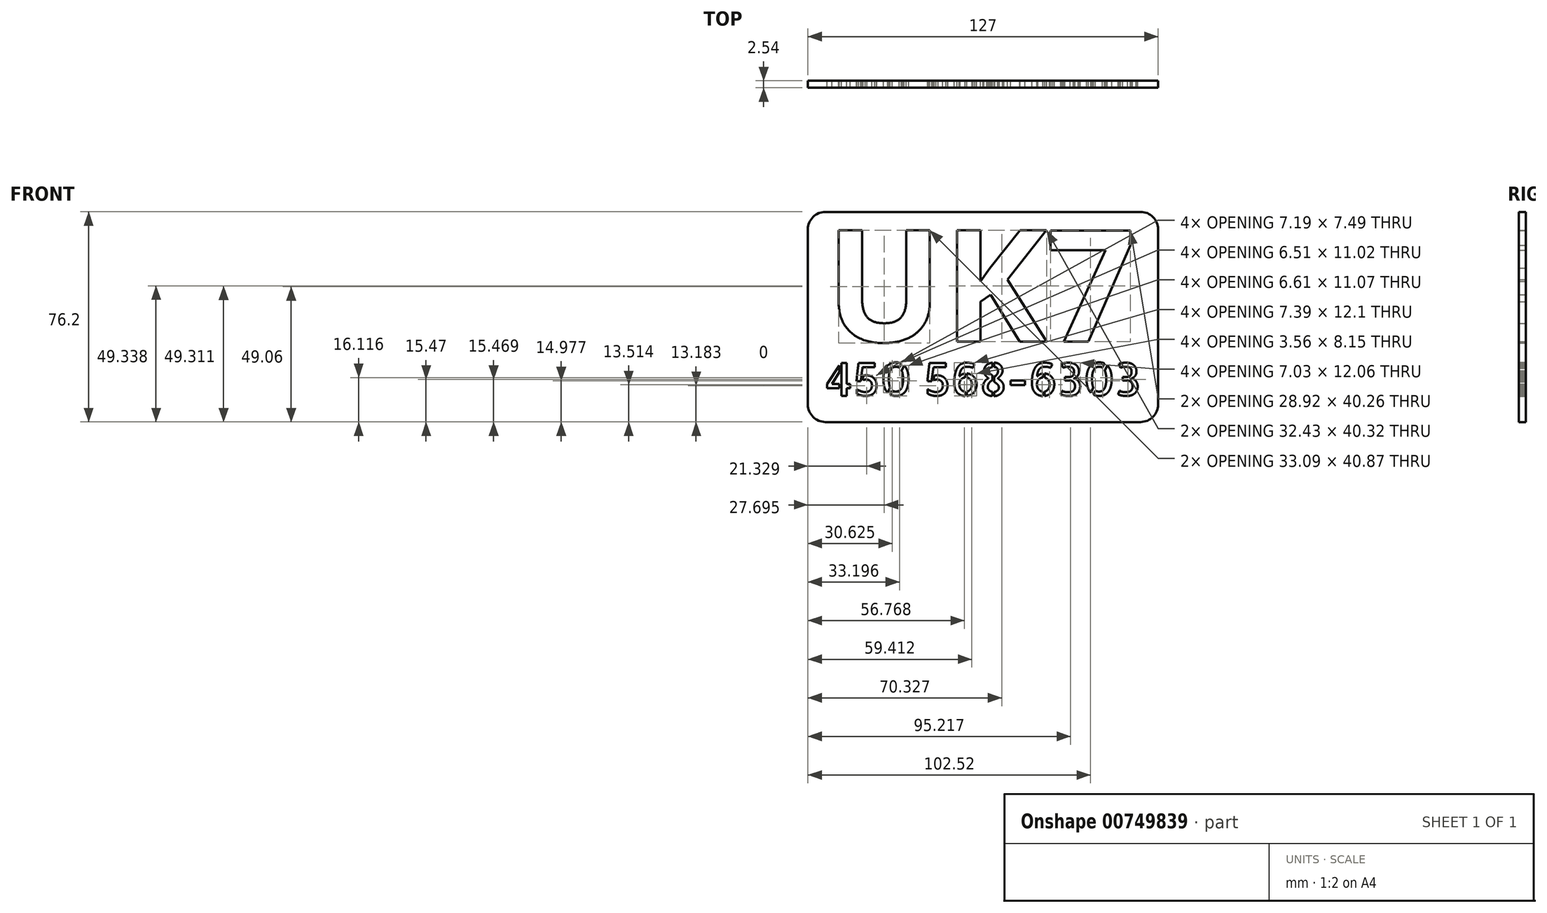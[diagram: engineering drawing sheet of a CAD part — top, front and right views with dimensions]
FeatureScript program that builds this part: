
annotation { "Feature Type Name" : "Feature", "Feature Type Description" : "" }
export const myFeature = defineFeature(function(context is Context, id is Id, definition is map)
    precondition{}
    {
        {
            var Q0;
            Q0=qCreatedBy(makeId("Front.planeOp"),FACE);
            var sketch = newSketch(context, id + "F0", { "sketchPlane" : qUnion([Q0])});
            skText(sketch, "E0", { "text": "UK7", "fontName": "OpenSans-Bold.ttf"});
            skLineSegment(sketch, "E1.bottom", {"start": v(-33.19, 30.09) * mm, "end": v(81.11, 30.09) * mm});
            skLineSegment(sketch, "E1.top", {"start": v(-33.19, -46.11) * mm, "end": v(81.11, -46.11) * mm});
            skLineSegment(sketch, "E1.left", {"start": v(-39.54, 23.74) * mm, "end": v(-39.54, -39.76) * mm});
            skLineSegment(sketch, "E1.right", {"start": v(87.46, 23.74) * mm, "end": v(87.46, -39.76) * mm});
            skPoint(sketch, "E2.visualSharp", {"position": v(-39.54, 30.09) * mm});
            skArc(sketch, "E2.filletArc", {"start": v(-33.19, 30.09) * mm, "mid": v(-37.68, 28.23) * mm, "end": v(-39.54, 23.74) * mm});
            skPoint(sketch, "E3.visualSharp", {"position": v(-39.54, -46.11) * mm});
            skArc(sketch, "E3.filletArc", {"start": v(-39.54, -39.76) * mm, "mid": v(-37.68, -44.25) * mm, "end": v(-33.19, -46.11) * mm});
            skPoint(sketch, "E4.visualSharp", {"position": v(87.46, -46.11) * mm});
            skArc(sketch, "E4.filletArc", {"start": v(81.11, -46.11) * mm, "mid": v(85.6, -44.25) * mm, "end": v(87.46, -39.76) * mm});
            skPoint(sketch, "E5.visualSharp", {"position": v(87.46, 30.09) * mm});
            skArc(sketch, "E5.filletArc", {"start": v(87.46, 23.74) * mm, "mid": v(85.6, 28.23) * mm, "end": v(81.11, 30.09) * mm});
            skText(sketch, "E6", { "text": "450 568-6303", "fontName": "AllertaStencil-Regular.ttf"});
            const initialGuessF0  = {"E0": [-0.03319, -0.01693, 1, 0, 0.04066], "E6": [-0.03319, -0.03659, 1, 0, 0.01192]};
            skSetInitialGuess(sketch, initialGuessF0);
            skSolve(sketch);
        }
        {
            var Q0;
            Q0=makeQuery(id+"F0.imprint","IMPRINT",FACE,{"disambiguationData":[TD([[makeQuery(id+"F0.imprint","IMPRINT",EDGE,{"derivedFrom":sQuery(id+"F0.wireOp",EDGE,"E0.sketch_text.stroke-0")}),1.0]])]});
            extrude(context, id + "F1", {"entities" : qUnion([Q0]), "depth" : 2.54 * mm, "offsetDistance" : 25.4 * mm});
        }
    });
